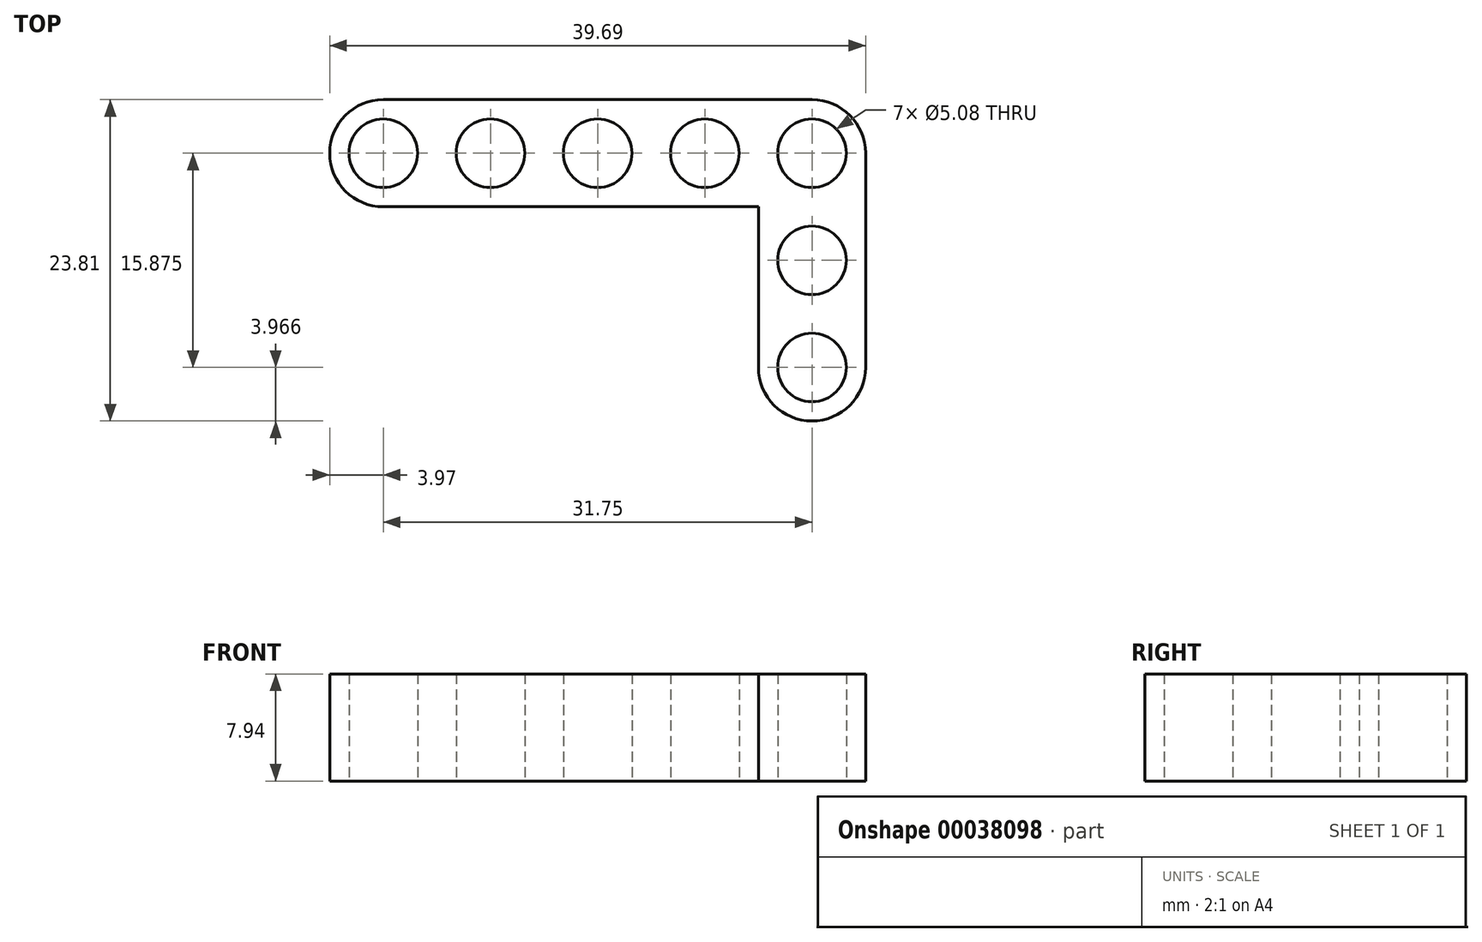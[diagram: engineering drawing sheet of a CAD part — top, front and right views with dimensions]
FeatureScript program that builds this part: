
annotation { "Feature Type Name" : "Feature", "Feature Type Description" : "" }
export const myFeature = defineFeature(function(context is Context, id is Id, definition is map)
    precondition{}
    {
        {
            var Q0;
            Q0=qCreatedBy(makeId("Top.planeOp"),FACE);
            var sketch = newSketch(context, id + "F0", { "sketchPlane" : qUnion([Q0])});
            skLineSegment(sketch, "E0.bottom", {"start": v(0, 0) * mm, "end": v(31.75, 0) * mm});
            skLineSegment(sketch, "E0.top", {"start": v(0, -7.94) * mm, "end": v(27.78, -7.94) * mm});
            skLineSegment(sketch, "E0.left", {"start": v(0, 0) * mm, "end": v(0, -7.94) * mm});
            skLineSegment(sketch, "E0.right", {"start": v(31.75, 0) * mm, "end": v(31.75, -7.94) * mm, "construction": true});
            skLineSegment(sketch, "E1", {"start": v(0, -3.97) * mm, "end": v(7.94, -3.97) * mm, "construction": true});
            skLineSegment(sketch, "E2", {"start": v(7.94, -3.97) * mm, "end": v(15.88, -3.97) * mm, "construction": true});
            skLineSegment(sketch, "E3", {"start": v(15.88, -3.97) * mm, "end": v(23.81, -3.97) * mm, "construction": true});
            skLineSegment(sketch, "E4", {"start": v(23.81, -3.97) * mm, "end": v(31.75, -3.97) * mm, "construction": true});
            skArc(sketch, "E5", {"start": v(0, 0) * mm, "mid": v(-3.97, -3.97) * mm, "end": v(0, -7.94) * mm});
            skArc(sketch, "E6", {"start": v(35.72, -3.97) * mm, "mid": v(34.56, -1.16) * mm, "end": v(31.75, 0) * mm});
            skCircle(sketch, "E7", {"center": v(0, -3.97) * mm, "radius": 2.54 * mm});
            skCircle(sketch, "E8", {"center": v(7.94, -3.97) * mm, "radius": 2.54 * mm});
            skCircle(sketch, "E9", {"center": v(15.88, -3.97) * mm, "radius": 2.54 * mm});
            skCircle(sketch, "E10", {"center": v(23.81, -3.97) * mm, "radius": 2.54 * mm});
            skCircle(sketch, "E11", {"center": v(31.75, -3.97) * mm, "radius": 2.54 * mm});
            skLineSegment(sketch, "E12", {"start": v(31.75, -7.94) * mm, "end": v(31.75, -15.87) * mm, "construction": true});
            skLineSegment(sketch, "E13", {"start": v(31.75, -15.87) * mm, "end": v(31.75, -23.81) * mm, "construction": true});
            skCircle(sketch, "E14", {"center": v(31.75, -11.9) * mm, "radius": 2.54 * mm});
            skCircle(sketch, "E15", {"center": v(31.75, -19.84) * mm, "radius": 2.54 * mm});
            skLineSegment(sketch, "E16", {"start": v(27.78, -7.94) * mm, "end": v(27.78, -19.84) * mm});
            skLineSegment(sketch, "E17", {"start": v(35.72, -3.97) * mm, "end": v(35.72, -19.84) * mm});
            skLineSegment(sketch, "E18", {"start": v(27.78, -19.84) * mm, "end": v(35.72, -19.84) * mm, "construction": true});
            skArc(sketch, "E19", {"start": v(27.78, -19.84) * mm, "mid": v(31.75, -23.81) * mm, "end": v(35.72, -19.84) * mm});
            skSolve(sketch);
        }
        {
            var Q0;
            Q0=qSketchRegion(id+"F0",true);
            extrude(context, id + "F1", {"entities" : qUnion([Q0]), "depth" : 7.94 * mm});
        }
    });
